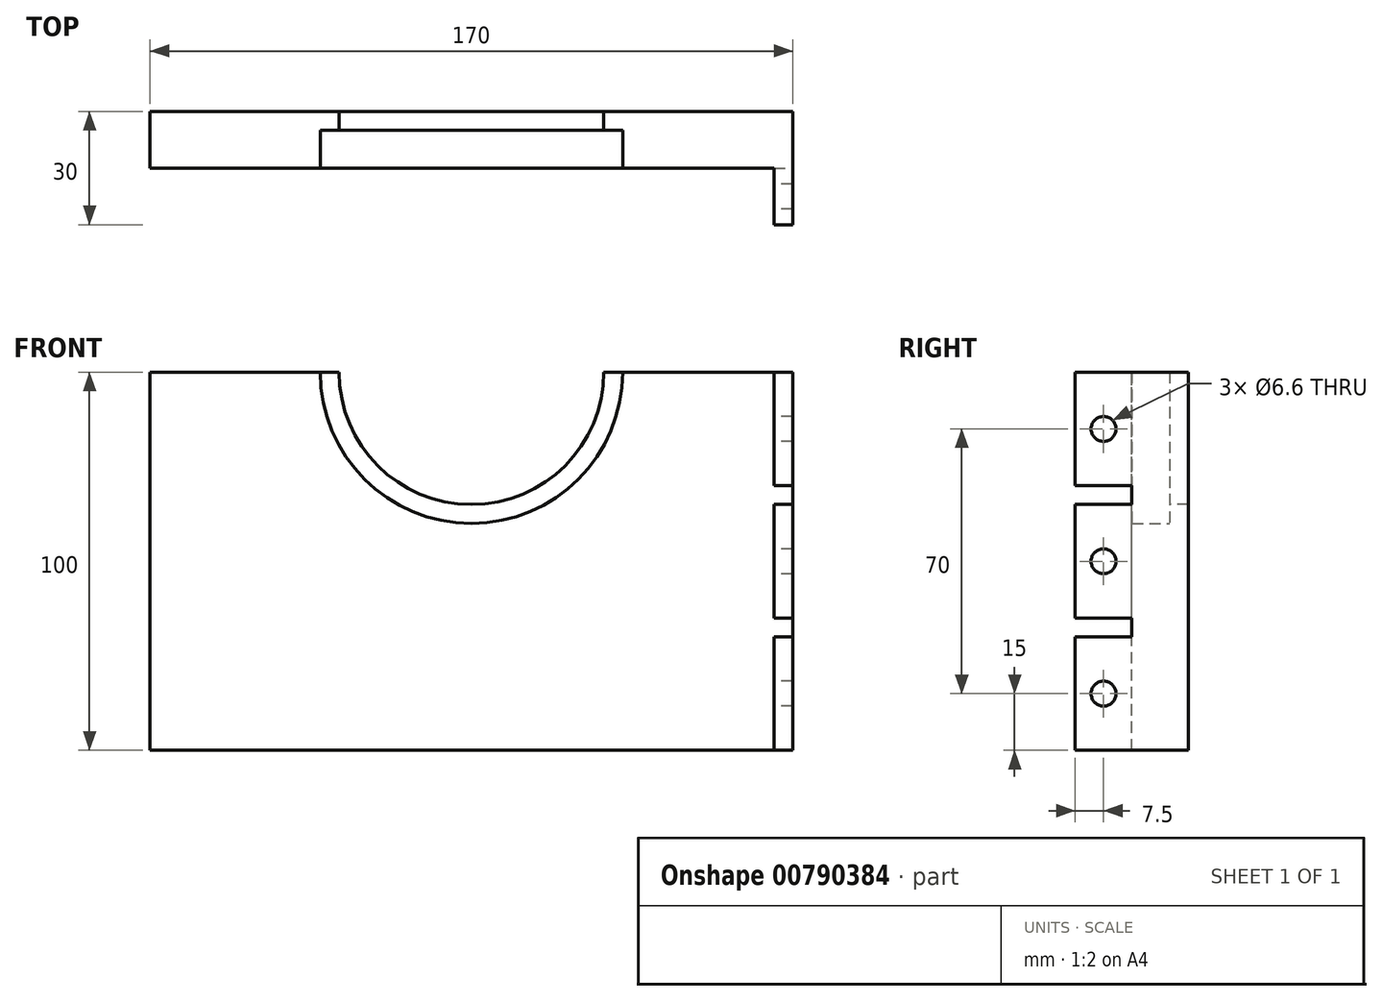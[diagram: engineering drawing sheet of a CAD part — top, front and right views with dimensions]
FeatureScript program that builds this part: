
annotation { "Feature Type Name" : "Feature", "Feature Type Description" : "" }
export const myFeature = defineFeature(function(context is Context, id is Id, definition is map)
    precondition{}
    {
        {
            var Q0;
            Q0=qCreatedBy(makeId("Front.planeOp"),FACE);
            var sketch = newSketch(context, id + "F0", { "sketchPlane" : qUnion([Q0])});
            skArc(sketch, "E0", {"start": v(-40, 40) * mm, "mid": v(0, 0) * mm, "end": v(40, 40) * mm});
            skLineSegment(sketch, "E1.top", {"start": v(85, 40) * mm, "end": v(40, 40) * mm});
            skLineSegment(sketch, "E1.left", {"start": v(85, -60) * mm, "end": v(85, 40) * mm});
            skLineSegment(sketch, "E1.right", {"start": v(-85, -60) * mm, "end": v(-85, 40) * mm});
            skPoint(sketch, "E1.middle", {"position": v(0, 0) * mm});
            skLineSegment(sketch, "E2.trimOffspring", {"start": v(-40, 40) * mm, "end": v(-85, 40) * mm});
            skLineSegment(sketch, "E3", {"start": v(-85, -60) * mm, "end": v(85, -60) * mm});
            skPoint(sketch, "E4", {"position": v(-62.5, 25) * mm});
            skPoint(sketch, "E5", {"position": v(62.5, 25) * mm});
            skPoint(sketch, "E6", {"position": v(62.5, -10) * mm});
            skPoint(sketch, "E7", {"position": v(-62.5, -10) * mm});
            skPoint(sketch, "E8", {"position": v(-62.5, -45) * mm});
            skPoint(sketch, "E9", {"position": v(62.5, -45) * mm});
            skPoint(sketch, "E10", {"position": v(0, -45) * mm});
            skPoint(sketch, "E11", {"position": v(-62.5, 40) * mm});
            skPoint(sketch, "E12", {"position": v(62.5, 40) * mm});
            skSolve(sketch);
        }
        {
            var Q0;
            Q0=makeQuery(id+"F0.imprint","IMPRINT",FACE,{"disambiguationData":[TD([[makeQuery(id+"F0.imprint","IMPRINT",EDGE,{"derivedFrom":sQuery(id+"F0.wireOp",EDGE,"E0")}),-1.0]])]});
            extrude(context, id + "F1", {"entities" : qUnion([Q0]), "depth" : 10 * mm, "offsetDistance" : 25 * mm});
        }
        {
            var Q0;
            Q0=makeQuery(id+"F1.opExtrude","CAP_FACE",FACE,{"disambiguationData":[OSD([sQuery(id+"F0.wireOp",EDGE,"E0"),sQuery(id+"F0.wireOp",EDGE,"E1.top"),sQuery(id+"F0.wireOp",EDGE,"E1.left"),sQuery(id+"F0.wireOp",EDGE,"E1.right"),sQuery(id+"F0.wireOp",EDGE,"E2.trimOffspring"),sQuery(id+"F0.wireOp",EDGE,"E3")])],"isStart":true});
            var sketch = newSketch(context, id + "F2", { "sketchPlane" : qUnion([Q0])});
            skArc(sketch, "E13", {"start": v(-35, 40) * mm, "mid": v(0, 5) * mm, "end": v(35, 40) * mm});
            skLineSegment(sketch, "E14", {"start": v(-40, 40) * mm, "end": v(40, 40) * mm, "construction": true});
            skLineSegment(sketch, "E15", {"start": v(-40, 40) * mm, "end": v(-35, 40) * mm});
            skLineSegment(sketch, "E16", {"start": v(40, 40) * mm, "end": v(35, 40) * mm});
            skSolve(sketch);
        }
        {
            var Q0;
            {var subQ5=sQuery(id+"F0.wireOp",EDGE,"E0");Q0=makeQuery(id+"F2.imprint","IMPRINT",FACE,{"disambiguationData":[TD([[makeQuery(id+"F2.imprint","IMPRINT",EDGE,{"derivedFrom":makeQuery(id+"F1.opExtrude","CAP_EDGE",EDGE,{"disambiguationData":[OSD([subQ5])],"isStart":true})}),1.0]])]});}
            var Q1;
            Q1=makeQuery(id+"F2.imprint","IMPRINT",FACE,{"disambiguationData":[TD([[makeQuery(id+"F2.imprint","IMPRINT",EDGE,{"derivedFrom":sQuery(id+"F2.wireOp",EDGE,"E13")}),-1.0]])]});
            extrude(context, id + "F3", {"entities" : qUnion([Q0, Q1]), "operationType" : NewBodyOperationType.ADD, "depth" : 5 * mm, "offsetDistance" : 25 * mm});
        }
        {
            var Q0;
            {var subQ0=sQuery(id+"F0.wireOp",EDGE,"E1.left");Q0=makeQuery(id+"F3.boolean.opBoolean","MERGE",FACE,{"derivedFrom":[makeQuery(id+"F1.opExtrude","SWEPT_FACE",FACE,{"disambiguationData":[OSD([subQ0])]}),makeQuery(id+"F3.opExtrude","SWEPT_FACE",FACE,{"disambiguationData":[OSD([subQ0])]})]});}
            var sketch = newSketch(context, id + "F4", { "sketchPlane" : qUnion([Q0])});
            skLineSegment(sketch, "E17.bottom", {"start": v(-25, 40) * mm, "end": v(-10, 40) * mm});
            skLineSegment(sketch, "E17.top", {"start": v(-25, 10) * mm, "end": v(-10, 10) * mm});
            skLineSegment(sketch, "E17.left", {"start": v(-10, 40) * mm, "end": v(-10, 10) * mm});
            skLineSegment(sketch, "E17.right", {"start": v(-25, 40) * mm, "end": v(-25, 10) * mm});
            skLineSegment(sketch, "E18.bottom", {"start": v(-25, 5) * mm, "end": v(-10, 5) * mm});
            skLineSegment(sketch, "E18.top", {"start": v(-25, -25) * mm, "end": v(-10, -25) * mm});
            skLineSegment(sketch, "E18.left", {"start": v(-10, 5) * mm, "end": v(-10, -25) * mm});
            skLineSegment(sketch, "E18.right", {"start": v(-25, 5) * mm, "end": v(-25, -25) * mm});
            skLineSegment(sketch, "E19.bottom", {"start": v(-25, -30) * mm, "end": v(-10, -30) * mm});
            skLineSegment(sketch, "E19.top", {"start": v(-25, -60) * mm, "end": v(-10, -60) * mm});
            skLineSegment(sketch, "E19.left", {"start": v(-10, -30) * mm, "end": v(-10, -60) * mm});
            skLineSegment(sketch, "E19.right", {"start": v(-25, -30) * mm, "end": v(-25, -60) * mm});
            skPoint(sketch, "E20", {"position": v(-25, 25) * mm});
            skPoint(sketch, "E21", {"position": v(-25, -10) * mm});
            skPoint(sketch, "E22", {"position": v(-25, -45) * mm});
            skPoint(sketch, "E23", {"position": v(-17.5, 25) * mm});
            skPoint(sketch, "E24", {"position": v(-17.5, -10) * mm});
            skPoint(sketch, "E25", {"position": v(-17.5, -45) * mm});
            skSolve(sketch);
        }
        {
            var Q0;
            Q0=makeQuery(id+"F4.imprint","IMPRINT",FACE,{"disambiguationData":[TD([[makeQuery(id+"F4.imprint","IMPRINT",EDGE,{"derivedFrom":sQuery(id+"F4.wireOp",EDGE,"E19.bottom")}),-1.0]])]});
            var Q1;
            Q1=makeQuery(id+"F4.imprint","IMPRINT",FACE,{"disambiguationData":[TD([[makeQuery(id+"F4.imprint","IMPRINT",EDGE,{"derivedFrom":sQuery(id+"F4.wireOp",EDGE,"E18.bottom")}),-1.0]])]});
            var Q2;
            Q2=makeQuery(id+"F4.imprint","IMPRINT",FACE,{"disambiguationData":[TD([[makeQuery(id+"F4.imprint","IMPRINT",EDGE,{"derivedFrom":sQuery(id+"F4.wireOp",EDGE,"E17.bottom")}),-1.0]])]});
            extrude(context, id + "F5", {"entities" : qUnion([Q0, Q1, Q2]), "operationType" : NewBodyOperationType.ADD, "oppositeDirection" : true, "depth" : 5 * mm, "offsetDistance" : 25 * mm});
        }
        {
            var Q0;
            Q0=sQuery(id+"F4.wireOp",VERTEX,"E23");
            var Q1;
            Q1=sQuery(id+"F4.wireOp",VERTEX,"E24");
            var Q2;
            Q2=sQuery(id+"F4.wireOp",VERTEX,"E25");
            var Q3;
            Q3=makeQuery(id+"F1.opExtrude","SWEPT_BODY",BODY,{"disambiguationData":[OSD([sQuery(id+"F0.wireOp",EDGE,"E0"),sQuery(id+"F0.wireOp",EDGE,"E1.top"),sQuery(id+"F0.wireOp",EDGE,"E1.left"),sQuery(id+"F0.wireOp",EDGE,"E1.right"),sQuery(id+"F0.wireOp",EDGE,"E2.trimOffspring"),sQuery(id+"F0.wireOp",EDGE,"E3")])]});
            hole(context, id + "F6", {"style" : HoleStyle.SIMPLE, "endStyle" : HoleEndStyle.BLIND, "standardTappedOrClearance" : lookupTablePath({ "standard" : "ISO", "fit" : "Normal", "size" : "M6", "type" : "Clearance" }), "standardBlindInLast" : lookupTablePath({ "fit" : "Standard", "standard" : "ISO", "size" : "M6", "type" : "Clearance" }), "holeDiameter" : 6.6 * mm, "majorDiameter" : 6 * mm, "holeDepth" : 14.25 * mm, "isTappedThrough" : true, "tappedDepth" : 11.25 * mm, "tapClearance" : 3, "startFromSketch" : true, "locations" : qUnion([Q0, Q1, Q2]), "scope" : qUnion([Q3])});
        }
    });
